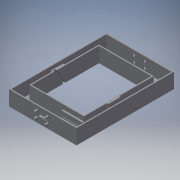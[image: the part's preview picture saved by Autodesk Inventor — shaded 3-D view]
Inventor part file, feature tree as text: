
AUTODESK INVENTOR PART (.ipt)
format: ipt  version: 2018.3 (Build 223284000, 284)  size: 688,640 bytes
history: native  units: mm
features: extrude x14, sketch x14, chamfer x3
ambient origin geometry x8: Origin, YZ Plane, XZ Plane, XY Plane, X Axis, Y Axis, Z Axis, Center Point
bodies: Solid1 (feature_tree)
feature tree (31):
  extrude  "Extrusion1"  Depth=130.0mm
  extrude  "Extrusion2"  Depth=90.0mm
  extrude  "Extrusion3"  TaperAngle=210.0deg  [1 undecoded]
  extrude  "Extrusion4"  Depth=2.1mm
  chamfer  "Chamfer1"  Distance=2.1mm
  extrude  "Extrusion5"  Depth=3.1mm
  chamfer  "Chamfer2"  Distance=2.1mm
  extrude  "Extrusion6"  Depth=20.0mm
  extrude  "Extrusion7"  Depth=20.0mm
  extrude  "Extrusion8"  Depth=3.0mm
  extrude  "Extrusion9"  Depth=35.0mm
  extrude  "Extrusion10"  Depth=35.0mm
  extrude  "Extrusion11"  Depth=1.1mm
  extrude  "Extrusion12"  Depth=12.11mm
  extrude  "Extrusion13"  Depth=2.0mm
  extrude  "Extrusion14"  Depth=2.0mm
  chamfer  "Chamfer3"  Distance=4.83mm
  sketch  "Sketch1"  dims[d0=90.0mm d1=130.0mm]
  sketch  "Sketch2"  dims[d2=70.0mm d3=90.0mm]
  sketch  "Sketch3"  dims[d4=20.0mm d5=0.0mm d6=210.0deg]
  sketch  "Sketch4"  dims[d7=3.1mm d8=26.471143mm d9=2.1mm d10=0.0mm]
  sketch  "Sketch5"  dims[d11=30.0deg d12=3.1mm]
  sketch  "Sketch6"  dims[d13=26.471143mm d14=2.1mm d15=0.0mm]
  sketch  "Sketch7"  dims[d16=20.0mm d17=20.0mm]
  sketch  "Sketch8"  dims[d18=10.0mm d19=20.0mm]
  sketch  "Sketch9"  dims[d20=14.0mm d21=3.0mm]
  sketch  "Sketch10"  dims[d22=3.0mm d23=35.0mm]
  sketch  "Sketch11"  dims[d24=35.0mm d25=1.45mm]
  sketch  "Sketch12"  dims[d26=1.45mm d27=1.1mm]
  sketch  "Sketch13"  dims[d28=1.1mm d29=12.11mm]
  sketch  "Sketch14"  dims[d30=1.13mm d31=1.13mm d32=4.83mm d33=4.83mm d34=1.129mm d35=1.128692mm d36=4.0mm d37=0.0mm d38=0.5mm d39=2.0mm d40=45.0deg d41=20.0mm d42=14.0mm d43=3.0mm d44=3.0mm d45=35.0mm d46=35.0mm d74=4.0mm d75=0.0mm d76=0.5mm d77=2.0mm d78=45.0deg d79=128.5mm d80=87.0mm d81=127.0mm d82=46.0mm d83=2.0mm d84=16.434mm d85=2.0mm d86=30.566mm d87=73.0mm d88=2.0mm d89=18.0mm d90=0.0mm d100=11.0mm d101=2.6mm d102=8.7mm d103=39.5mm d104=39.5mm d105=8.7mm d106=10.0mm d107=0.0mm d108=28.0mm d109=6.0mm d110=2.2mm d111=0.0mm d114=28.0mm d115=12.0mm d116=7.0mm d117=2.2mm d118=0.0mm d119=1.0mm d120=0.0mm d121=8.8mm d122=1.0mm d123=6.0mm d124=0.55mm d125=0.0mm d126=0.6mm d127=0.0mm d128=1.0mm d129=1.0mm d130=6.2mm d131=1.8mm d132=0.55mm d133=0.0mm d134=0.6mm d135=0.0mm d136=7.0mm d137=0.0mm d138=6.0mm d139=2.0mm d140=1.745329mm d141=1.45mm d142=2.15mm d143=1.13mm d144=2.15mm d145=1.13mm d146=1.1mm d148=2.15mm d149=1.1mm d150=1.128mm d151=4.83298mm d153=12.113227mm d154=2.15mm d155=1.128mm d156=1.45mm d157=4.83298mm d158=12.113227mm]
note: 1 required parameter value undecoded (feature->parameter linkage not recoverable at this tier; creation-order binding heuristic only, values carry confidence <= 0.55)
